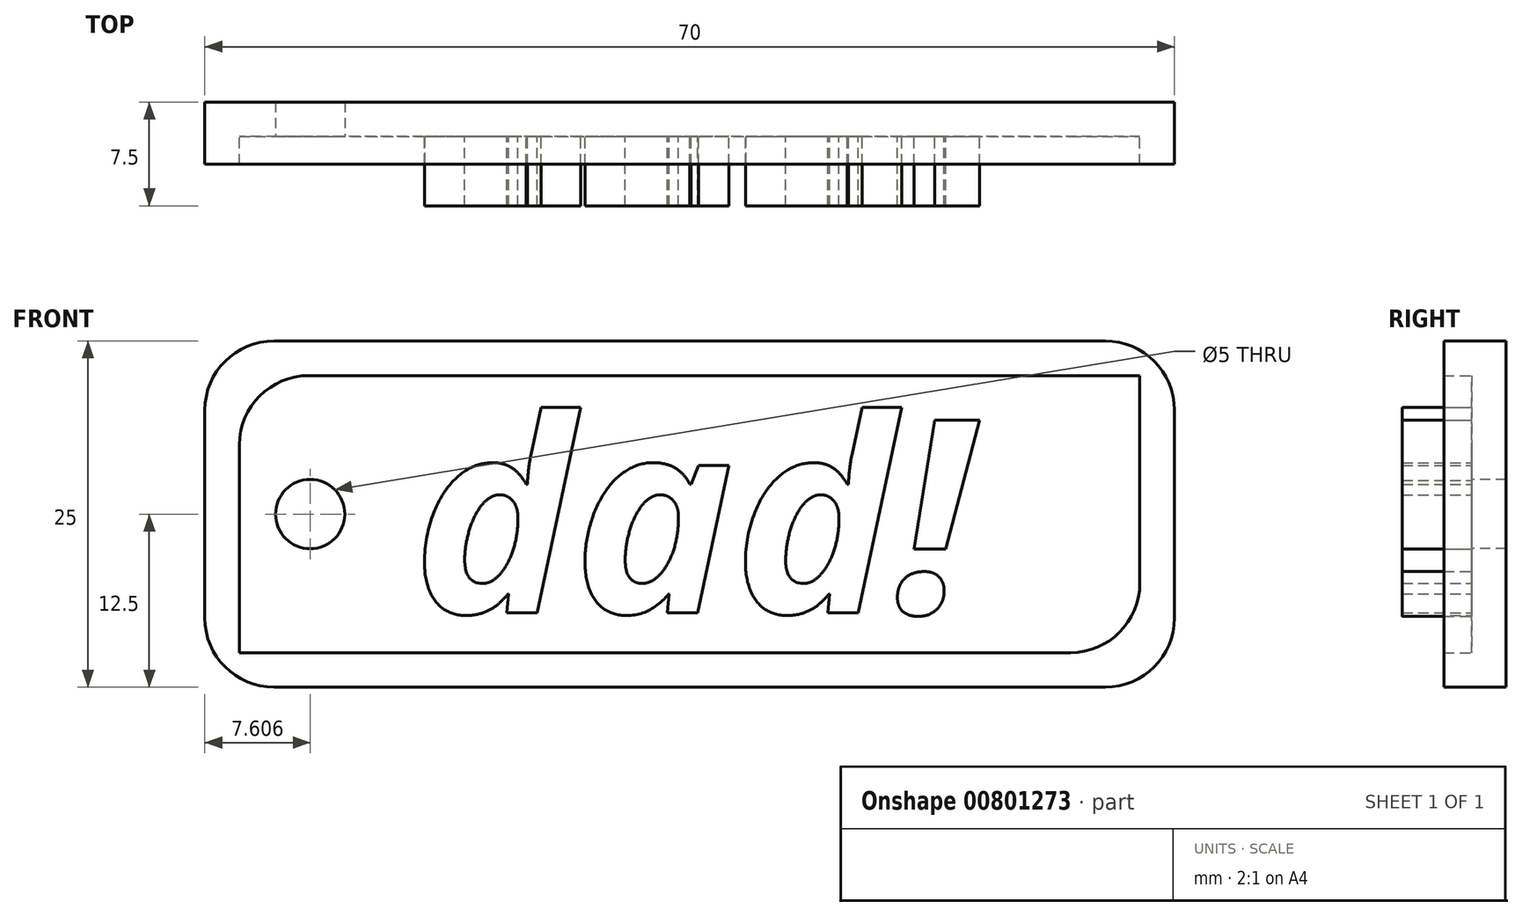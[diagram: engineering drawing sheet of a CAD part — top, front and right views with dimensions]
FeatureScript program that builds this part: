
annotation { "Feature Type Name" : "Feature", "Feature Type Description" : "" }
export const myFeature = defineFeature(function(context is Context, id is Id, definition is map)
    precondition{}
    {
        {
            var Q0;
            Q0=qCreatedBy(makeId("Front.planeOp"),FACE);
            var sketch = newSketch(context, id + "F0", { "sketchPlane" : qUnion([Q0])});
            skLineSegment(sketch, "E0", {"start": v(0, 5) * mm, "end": v(0, 20) * mm});
            skLineSegment(sketch, "E1", {"start": v(5, 25) * mm, "end": v(65, 25) * mm});
            skLineSegment(sketch, "E2", {"start": v(70, 20) * mm, "end": v(70, 5) * mm});
            skLineSegment(sketch, "E3", {"start": v(5, 0) * mm, "end": v(65, 0) * mm});
            skPoint(sketch, "E4.visualSharp", {"position": v(0, 25) * mm});
            skArc(sketch, "E4.filletArc", {"start": v(5, 25) * mm, "mid": v(1.46, 23.54) * mm, "end": v(0, 20) * mm});
            skPoint(sketch, "E5.visualSharp", {"position": v(0, 0) * mm});
            skArc(sketch, "E5.filletArc", {"start": v(0, 5) * mm, "mid": v(1.46, 1.46) * mm, "end": v(5, 0) * mm});
            skPoint(sketch, "E6.visualSharp", {"position": v(70, 0) * mm});
            skArc(sketch, "E6.filletArc", {"start": v(65, 0) * mm, "mid": v(68.54, 1.46) * mm, "end": v(70, 5) * mm});
            skPoint(sketch, "E7.visualSharp", {"position": v(70, 25) * mm});
            skArc(sketch, "E7.filletArc", {"start": v(70, 20) * mm, "mid": v(68.54, 23.54) * mm, "end": v(65, 25) * mm});
            skSolve(sketch);
        }
        {
            var Q0;
            Q0=makeQuery(id+"F0.imprint","IMPRINT",FACE,{"disambiguationData":[TD([[makeQuery(id+"F0.imprint","IMPRINT",EDGE,{"derivedFrom":sQuery(id+"F0.wireOp",EDGE,"E0")}),-1.0]])]});
            extrude(context, id + "F1", {"entities" : qUnion([Q0]), "depth" : 2.5 * mm, "offsetDistance" : 25 * mm});
        }
        {
            var Q0;
            Q0=makeQuery(id+"F1.opExtrude","CAP_FACE",FACE,{"disambiguationData":[OSD([sQuery(id+"F0.wireOp",EDGE,"E0"),sQuery(id+"F0.wireOp",EDGE,"E1"),sQuery(id+"F0.wireOp",EDGE,"E2"),sQuery(id+"F0.wireOp",EDGE,"E3"),sQuery(id+"F0.wireOp",EDGE,"E4.filletArc"),sQuery(id+"F0.wireOp",EDGE,"E5.filletArc"),sQuery(id+"F0.wireOp",EDGE,"E6.filletArc"),sQuery(id+"F0.wireOp",EDGE,"E7.filletArc")])],"isStart":false});
            var sketch = newSketch(context, id + "F2", { "sketchPlane" : qUnion([Q0])});
            skLineSegment(sketch, "E8.0", {"start": v(67.5, 7.5) * mm, "end": v(67.5, 22.5) * mm});
            skLineSegment(sketch, "E8.1", {"start": v(2.5, 2.5) * mm, "end": v(62.5, 2.5) * mm});
            skLineSegment(sketch, "E8.2", {"start": v(2.5, 17.5) * mm, "end": v(2.5, 2.5) * mm});
            skLineSegment(sketch, "E8.3", {"start": v(67.5, 22.5) * mm, "end": v(7.5, 22.5) * mm});
            skPoint(sketch, "E9.visualSharp", {"position": v(2.5, 22.5) * mm});
            skArc(sketch, "E9.filletArc", {"start": v(7.5, 22.5) * mm, "mid": v(3.96, 21.04) * mm, "end": v(2.5, 17.5) * mm});
            skPoint(sketch, "E10.visualSharp", {"position": v(67.5, 2.5) * mm});
            skArc(sketch, "E10.filletArc", {"start": v(62.5, 2.5) * mm, "mid": v(66.04, 3.96) * mm, "end": v(67.5, 7.5) * mm});
            skSolve(sketch);
        }
        {
            var Q0;
            Q0=makeQuery(id+"F2.imprint","IMPRINT",FACE,{"disambiguationData":[TD([[makeQuery(id+"F2.imprint","IMPRINT",EDGE,{"derivedFrom":sQuery(id+"F2.wireOp",EDGE,"E8.0")}),-1.0]])]});
            extrude(context, id + "F3", {"entities" : qUnion([Q0]), "operationType" : NewBodyOperationType.ADD, "depth" : 2 * mm, "offsetDistance" : 25 * mm});
        }
        {
            var Q0;
            Q0=makeQuery(id+"F1.opExtrude","CAP_FACE",FACE,{"disambiguationData":[OSD([sQuery(id+"F0.wireOp",EDGE,"E0"),sQuery(id+"F0.wireOp",EDGE,"E1"),sQuery(id+"F0.wireOp",EDGE,"E2"),sQuery(id+"F0.wireOp",EDGE,"E3"),sQuery(id+"F0.wireOp",EDGE,"E4.filletArc"),sQuery(id+"F0.wireOp",EDGE,"E5.filletArc"),sQuery(id+"F0.wireOp",EDGE,"E6.filletArc"),sQuery(id+"F0.wireOp",EDGE,"E7.filletArc")])],"isStart":false});
            var sketch = newSketch(context, id + "F4", { "sketchPlane" : qUnion([Q0])});
            skText(sketch, "E11", { "text": "dad!\n", "fontName": "OpenSans-BoldItalic.ttf"});
            const initialGuessF4  = {"E11": [0.015, 0.00537, 1, 0, 0.01404]};
            skSetInitialGuess(sketch, initialGuessF4);
            skSolve(sketch);
        }
        {
            var Q0;
            Q0 = qSketchRegion(id + "F4", true);
            extrude(context, id + "F5", {"entities" : qUnion([Q0]), "operationType" : NewBodyOperationType.ADD, "depth" : 5 * mm, "offsetDistance" : 25 * mm});
        }
        {
            var Q0;
            Q0=makeQuery(id+"F3.opExtrude","CAP_FACE",FACE,{"disambiguationData":[OSD([sQuery(id+"F0.wireOp",EDGE,"E0"),sQuery(id+"F0.wireOp",EDGE,"E1"),sQuery(id+"F0.wireOp",EDGE,"E2"),sQuery(id+"F0.wireOp",EDGE,"E3"),sQuery(id+"F0.wireOp",EDGE,"E4.filletArc"),sQuery(id+"F0.wireOp",EDGE,"E5.filletArc"),sQuery(id+"F0.wireOp",EDGE,"E6.filletArc"),sQuery(id+"F0.wireOp",EDGE,"E7.filletArc"),sQuery(id+"F2.wireOp",EDGE,"E8.0"),sQuery(id+"F2.wireOp",EDGE,"E8.1"),sQuery(id+"F2.wireOp",EDGE,"E8.2"),sQuery(id+"F2.wireOp",EDGE,"E8.3"),sQuery(id+"F2.wireOp",EDGE,"E9.filletArc"),sQuery(id+"F2.wireOp",EDGE,"E10.filletArc")])],"isStart":false});
            var sketch = newSketch(context, id + "F6", { "sketchPlane" : qUnion([Q0])});
            skCircle(sketch, "E12", {"center": v(7.6, 12.5) * mm, "radius": 2.94 * mm});
            skPoint(sketch, "E12.centerSnap0", {"position": v(0, 12.5) * mm});
            skSolve(sketch);
        }
        {
            var Q0;
            Q0=sQuery(id+"F6.wireOp",VERTEX,"E12.center");
            var Q1;
            Q1=makeQuery(id+"F1.opExtrude","SWEPT_BODY",BODY,{"disambiguationData":[OSD([sQuery(id+"F0.wireOp",EDGE,"E0"),sQuery(id+"F0.wireOp",EDGE,"E1"),sQuery(id+"F0.wireOp",EDGE,"E2"),sQuery(id+"F0.wireOp",EDGE,"E3"),sQuery(id+"F0.wireOp",EDGE,"E4.filletArc"),sQuery(id+"F0.wireOp",EDGE,"E5.filletArc"),sQuery(id+"F0.wireOp",EDGE,"E6.filletArc"),sQuery(id+"F0.wireOp",EDGE,"E7.filletArc")])]});
            hole(context, id + "F7", {"style" : HoleStyle.SIMPLE, "endStyle" : HoleEndStyle.THROUGH, "holeDiameter" : 5 * mm, "majorDiameter" : 5 * mm, "isTappedThrough" : true, "tappedDepth" : 12 * mm, "tapClearance" : 3, "locations" : qUnion([Q0]), "scope" : qUnion([Q1])});
        }
    });
